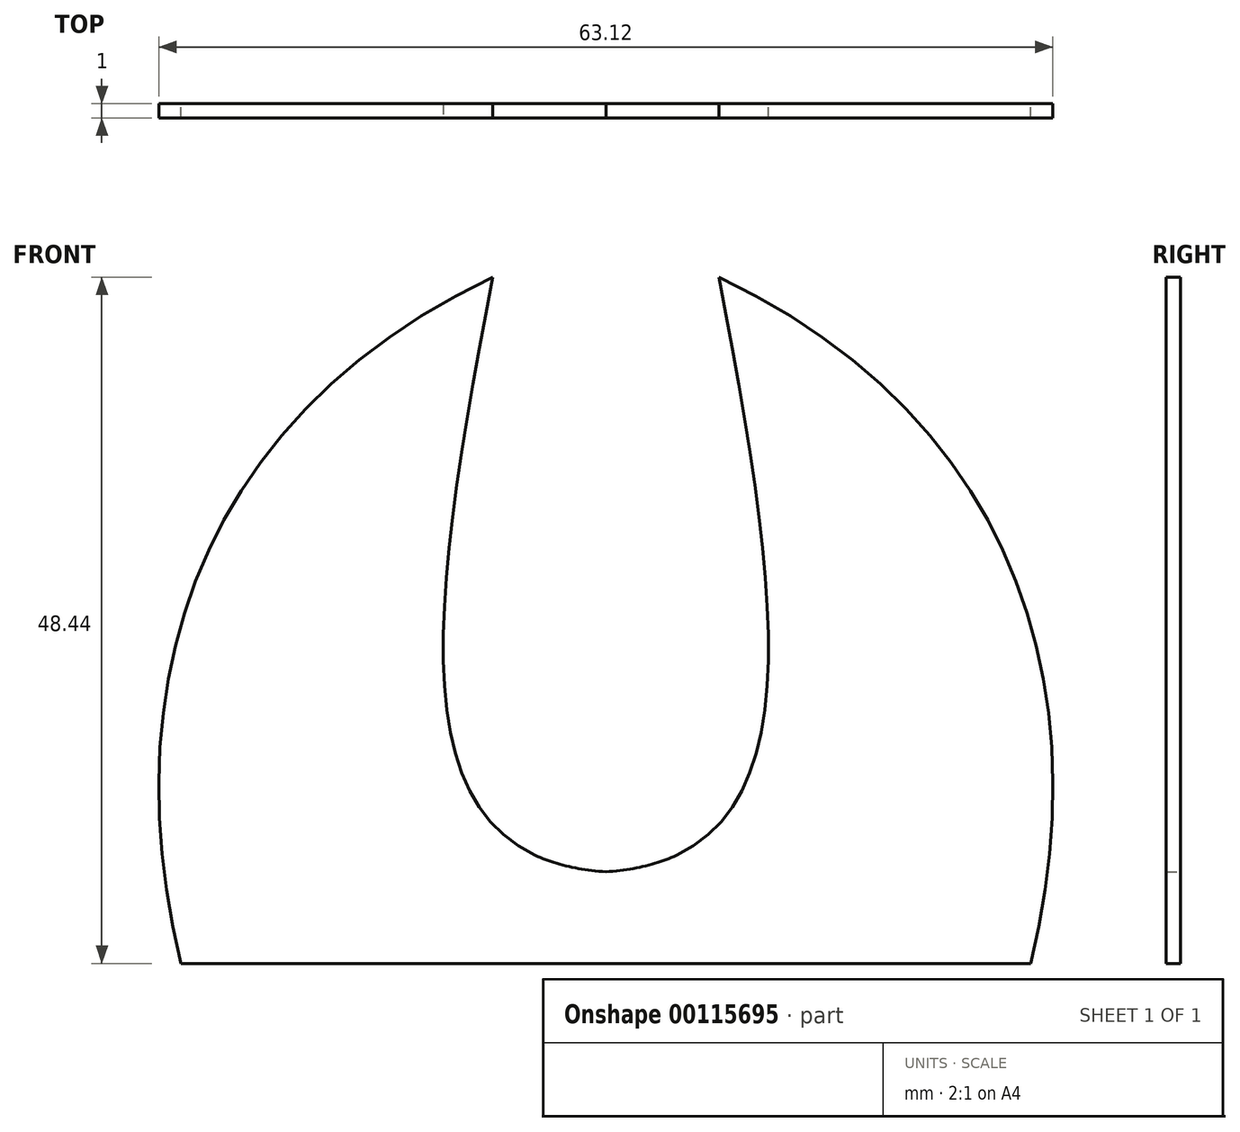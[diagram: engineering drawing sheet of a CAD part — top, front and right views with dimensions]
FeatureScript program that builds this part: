
annotation { "Feature Type Name" : "Feature", "Feature Type Description" : "" }
export const myFeature = defineFeature(function(context is Context, id is Id, definition is map)
    precondition{}
    {
        {
            var Q0;
            Q0=qCreatedBy(makeId("Front.planeOp"),FACE);
            var sketch = newSketch(context, id + "F0", { "sketchPlane" : qUnion([Q0])});
            skLineSegment(sketch, "E0", {"start": v(-30, 0) * mm, "end": v(30, 0) * mm});
            skFitSpline(sketch, "E1", {"points": [v(-30, 0) * mm, v(-8, 48.44) * mm], "startDerivative": vector(-14.64, 59.98) * mm, "endDerivative": vector(61.44, 29.2) * mm});
            skFitSpline(sketch, "E2.MirrorCS", {"points": [v(30, 0) * mm, v(8, 48.44) * mm], "startDerivative": vector(14.64, 59.98) * mm, "endDerivative": vector(-61.44, 29.2) * mm});
            skFitSpline(sketch, "E3", {"points": [v(-8, 48.44) * mm, v(0, 6.46) * mm], "startDerivative": vector(-12.6, -68.12) * mm, "endDerivative": vector(46.26, -2.94) * mm});
            skFitSpline(sketch, "E4.MirrorCS", {"points": [v(8, 48.44) * mm, v(0, 6.46) * mm], "startDerivative": vector(12.6, -68.12) * mm, "endDerivative": vector(-46.26, -2.94) * mm});
            skLineSegment(sketch, "E5", {"start": v(-5, 7.64) * mm, "end": v(-15, 0) * mm});
            skLineSegment(sketch, "E6.MirrorCS", {"start": v(5, 7.64) * mm, "end": v(15, 0) * mm});
            skSolve(sketch);
        }
        {
            var Q0;
            Q0=makeQuery(id+"F0.imprint","IMPRINT",FACE,{"disambiguationData":[TD([[makeQuery(id+"F0.imprint","IMPRINT",EDGE,{"derivedFrom":sQuery(id+"F0.wireOp",EDGE,"E0")}),1.0]])]});
            var Q1;
            {var subQ0=sQuery(id+"F0.wireOp",EDGE,"E5");Q1=makeQuery(id+"F0.imprint","IMPRINT",FACE,{"disambiguationData":[TD([[makeQuery(id+"F0.imprint","IMPRINT",EDGE,{"derivedFrom":subQ0}),1.0]])]});}
            var Q2;
            {var subQ0=sQuery(id+"F0.wireOp",EDGE,"E1");Q2=makeQuery(id+"F0.imprint","IMPRINT",FACE,{"disambiguationData":[TD([[makeQuery(id+"F0.imprint","IMPRINT",EDGE,{"derivedFrom":subQ0}),-1.0]])]});}
            extrude(context, id + "F1", {"entities" : qUnion([Q0, Q1, Q2]), "depth" : 1 * mm});
        }
    });
